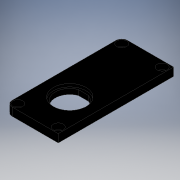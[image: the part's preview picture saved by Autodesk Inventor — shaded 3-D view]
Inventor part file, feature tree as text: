
AUTODESK INVENTOR PART (.ipt)
format: ipt  version: 2019 (Build 230136000, 136)  size: 160,256 bytes
history: native  units: mm
features: other x4, extrude x2, fillet x1, hole x1
ambient origin geometry x8: Origin, YZ Plane, XZ Plane, XY Plane, X Axis, Y Axis, Z Axis, Center Point
bodies: Solid1 (feature_tree), Body (feature_tree)
feature tree (8):
  extrude  "Connector Hole"  Depth=45.0mm
  extrude  "Connector Face Hole"  Depth=22.5mm
  fillet  "Body Fillet"  Radius=100.0mm
  hole  "Lid Fastening Holes"  [1 undecoded]
  other  "Body Outline"
  other  "Connector Hole Cross Section"
  other  "Connector Face Hole Cross Section"
  other  "Lid Fastening Hole Pattern"
note: 1 required parameter value undecoded (feature->parameter linkage not recoverable at this tier; creation-order binding heuristic only, values carry confidence <= 0.55)
